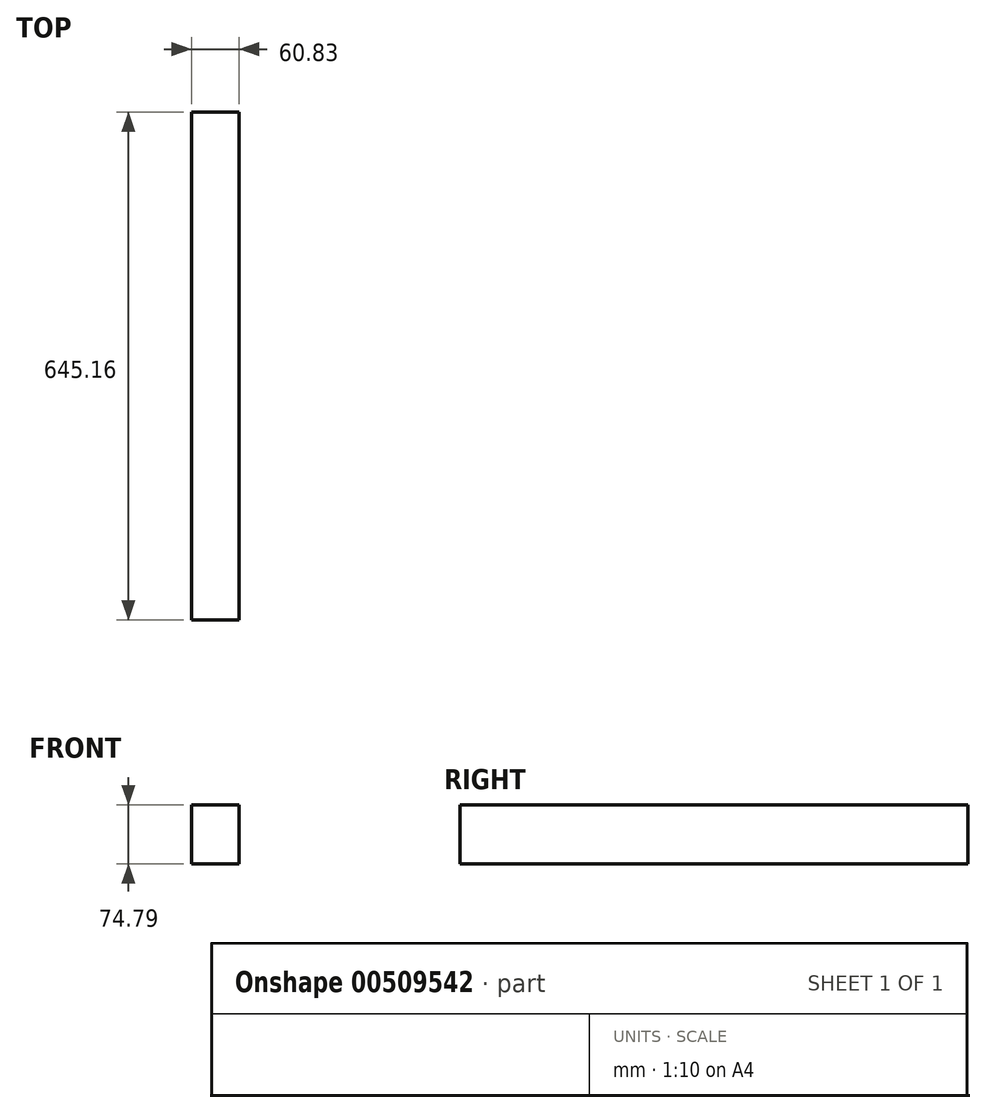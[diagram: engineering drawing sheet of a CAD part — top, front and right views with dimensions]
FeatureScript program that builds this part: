
annotation { "Feature Type Name" : "Feature", "Feature Type Description" : "" }
export const myFeature = defineFeature(function(context is Context, id is Id, definition is map)
    precondition{}
    {
        {
            var Q0;
            Q0=qCreatedBy(makeId("Front.planeOp"),FACE);
            var sketch = newSketch(context, id + "F0", { "sketchPlane" : qUnion([Q0])});
            skLineSegment(sketch, "E0.bottom", {"start": v(-55.16, 52.16) * mm, "end": v(5.67, 52.16) * mm});
            skLineSegment(sketch, "E0.top", {"start": v(-55.16, -22.63) * mm, "end": v(5.67, -22.63) * mm});
            skLineSegment(sketch, "E0.left", {"start": v(-55.16, 52.16) * mm, "end": v(-55.16, -22.63) * mm});
            skLineSegment(sketch, "E0.right", {"start": v(5.67, 52.16) * mm, "end": v(5.67, -22.63) * mm});
            skSolve(sketch);
        }
        {
            var Q0;
            Q0=makeQuery(id+"F0.imprint","IMPRINT",FACE,{"disambiguationData":[TD([[makeQuery(id+"F0.imprint","IMPRINT",EDGE,{"derivedFrom":sQuery(id+"F0.wireOp",EDGE,"E0.bottom")}),-1.0]])]});
            extrude(context, id + "F1", {"entities" : qUnion([Q0]), "depth" : 645.16 * mm});
        }
    });
